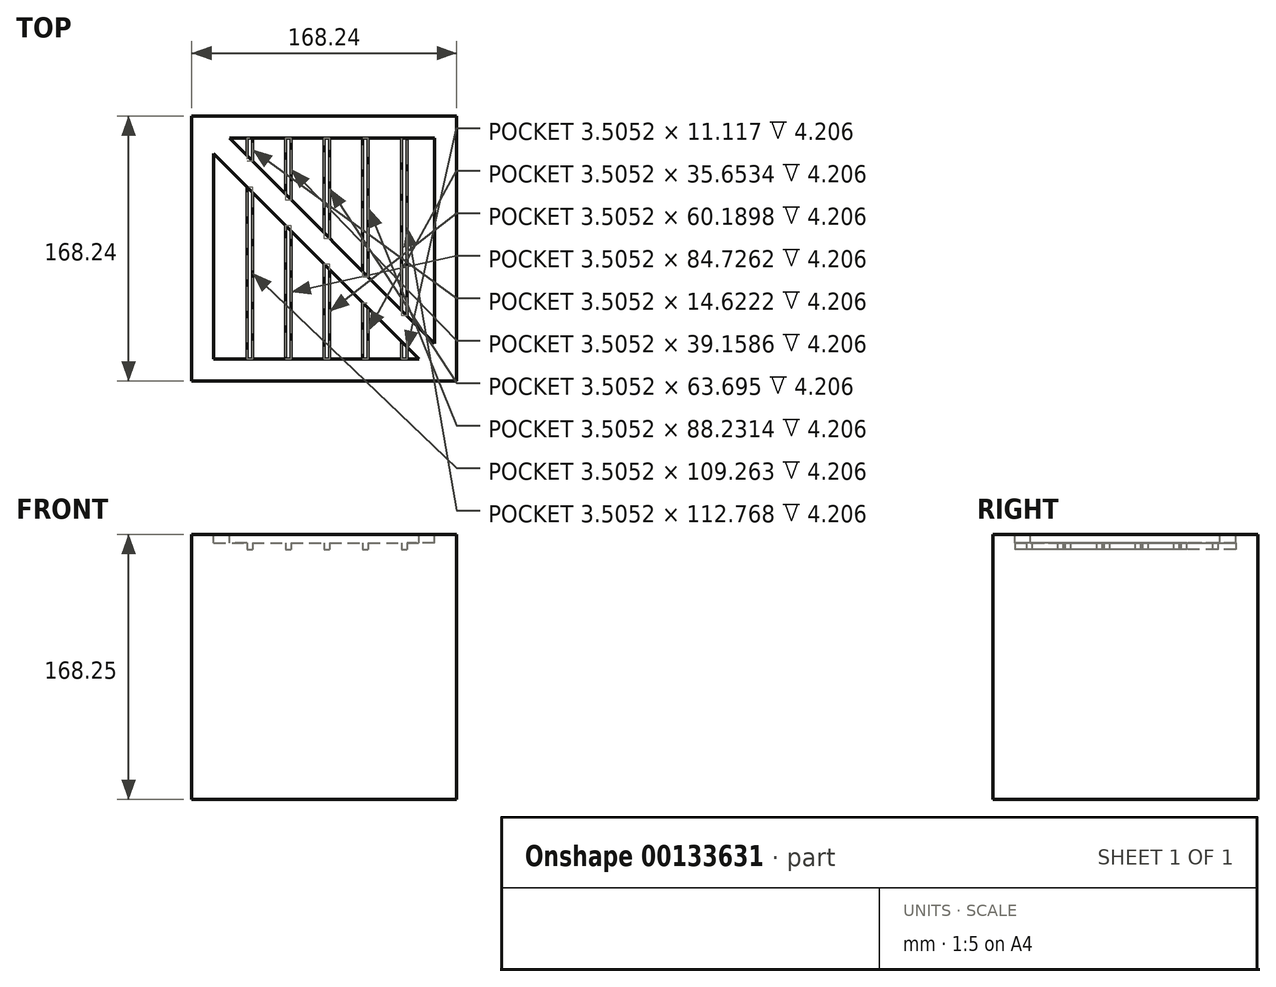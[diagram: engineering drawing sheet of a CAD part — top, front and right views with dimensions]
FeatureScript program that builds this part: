
annotation { "Feature Type Name" : "Feature", "Feature Type Description" : "" }
export const myFeature = defineFeature(function(context is Context, id is Id, definition is map)
    precondition{}
    {
        {
            var Q0;
            Q0=qCreatedBy(makeId("Top.planeOp"),FACE);
            var sketch = newSketch(context, id + "F0", { "sketchPlane" : qUnion([Q0])});
            skLineSegment(sketch, "E0.bottom", {"start": v(609.6, 609.6) * mm, "end": v(-609.6, 609.6) * mm});
            skLineSegment(sketch, "E0.top", {"start": v(609.6, -609.6) * mm, "end": v(-609.6, -609.6) * mm});
            skLineSegment(sketch, "E0.left", {"start": v(609.6, 609.6) * mm, "end": v(609.6, -609.6) * mm});
            skLineSegment(sketch, "E0.right", {"start": v(-609.6, 609.6) * mm, "end": v(-609.6, -609.6) * mm});
            skPoint(sketch, "E0.middle", {"position": v(0, 0) * mm});
            skSolve(sketch);
        }
        {
            var Q0;
            Q0=qSketchRegion(id+"F0",true);
            extrude(context, id + "F1", {"entities" : qUnion([Q0]), "flatOperationType" : FlatOperationType.REMOVE, "offsetDistance" : 30.48 * mm, "depth" : 1219.2 * mm, "domain" : OperationDomain.MODEL});
        }
        {
            var Q0;
            Q0=makeQuery(id+"F1.opExtrude","CAP_FACE",FACE,{"disambiguationData":[OSD([sQuery(id+"F0.wireOp",EDGE,"E0.bottom"),sQuery(id+"F0.wireOp",EDGE,"E0.top"),sQuery(id+"F0.wireOp",EDGE,"E0.left"),sQuery(id+"F0.wireOp",EDGE,"E0.right")])],"isStart":false});
            var sketch = newSketch(context, id + "F2", { "sketchPlane" : qUnion([Q0])});
            skLineSegment(sketch, "E1.0", {"start": v(508, -508) * mm, "end": v(508, 508) * mm});
            skLineSegment(sketch, "E1.1", {"start": v(-508, -508) * mm, "end": v(508, -508) * mm});
            skLineSegment(sketch, "E1.2", {"start": v(-508, 508) * mm, "end": v(-508, -508) * mm});
            skLineSegment(sketch, "E1.3", {"start": v(508, 508) * mm, "end": v(-508, 508) * mm});
            skSolve(sketch);
        }
        {
            var Q0;
            Q0=qSketchRegion(id+"F2",true);
            extrude(context, id + "F3", {"entities" : qUnion([Q0]), "operationType" : NewBodyOperationType.REMOVE, "flatOperationType" : FlatOperationType.REMOVE, "oppositeDirection" : true, "offsetDistance" : 30.48 * mm, "depth" : 69.85 * mm, "domain" : OperationDomain.MODEL});
        }
        {
            var Q0;
            Q0=makeQuery(id+"F1.opExtrude","CAP_FACE",FACE,{"disambiguationData":[OSD([sQuery(id+"F0.wireOp",EDGE,"E0.bottom"),sQuery(id+"F0.wireOp",EDGE,"E0.top"),sQuery(id+"F0.wireOp",EDGE,"E0.left"),sQuery(id+"F0.wireOp",EDGE,"E0.right")])],"isStart":false});
            var sketch = newSketch(context, id + "F4", { "sketchPlane" : qUnion([Q0])});
            skLineSegment(sketch, "E2", {"start": v(-436.16, 508) * mm, "end": v(508, -436.16) * mm});
            skLineSegment(sketch, "E3", {"start": v(-508, 436.16) * mm, "end": v(436.16, -508) * mm});
            skLineSegment(sketch, "E4", {"start": v(-436.16, 508) * mm, "end": v(-508, 508) * mm});
            skLineSegment(sketch, "E5", {"start": v(-508, 508) * mm, "end": v(-508, 436.16) * mm});
            skLineSegment(sketch, "E6", {"start": v(436.16, -508) * mm, "end": v(508, -508) * mm});
            skLineSegment(sketch, "E7", {"start": v(508, -508) * mm, "end": v(508, -436.16) * mm});
            skSolve(sketch);
        }
        {
            var Q0;
            Q0=makeQuery(id+"F4.imprint","IMPRINT",FACE,{"disambiguationData":[TD([[makeQuery(id+"F4.imprint","IMPRINT",EDGE,{"derivedFrom":sQuery(id+"F4.wireOp",EDGE,"E2")}),-1.0]])]});
            extrude(context, id + "F5", {"entities" : qUnion([Q0]), "oppositeDirection" : true, "depth" : 69.85 * mm});
        }
        {
            var Q0;
            Q0=makeQuery(id+"F3.boolean.opBoolean","COPY",FACE,{"derivedFrom":makeQuery(id+"F3.opExtrude","CAP_FACE",FACE,{"disambiguationData":[OSD([sQuery(id+"F2.wireOp",EDGE,"E1.0"),sQuery(id+"F2.wireOp",EDGE,"E1.1"),sQuery(id+"F2.wireOp",EDGE,"E1.2"),sQuery(id+"F2.wireOp",EDGE,"E1.3")])],"isStart":false})});
            var sketch = newSketch(context, id + "F6", { "sketchPlane" : qUnion([Q0])});
            skLineSegment(sketch, "E8.bottom", {"start": v(-508, 508) * mm, "end": v(-355.6, 508) * mm});
            skLineSegment(sketch, "E8.top", {"start": v(-508, -508) * mm, "end": v(-355.6, -508) * mm});
            skLineSegment(sketch, "E8.left", {"start": v(-508, 508) * mm, "end": v(-508, -508) * mm});
            skLineSegment(sketch, "E8.right", {"start": v(-355.6, 508) * mm, "end": v(-355.6, -508) * mm});
            skLineSegment(sketch, "E9.1.0.0", {"start": v(-330.2, 508) * mm, "end": v(-330.2, -508) * mm});
            skLineSegment(sketch, "E9.1.0.1", {"start": v(-177.8, 508) * mm, "end": v(-177.8, -508) * mm});
            skLineSegment(sketch, "E9.2.0.0", {"start": v(-152.4, 508) * mm, "end": v(-152.4, -508) * mm});
            skLineSegment(sketch, "E9.2.0.1", {"start": v(0, 508) * mm, "end": v(0, -508) * mm});
            skLineSegment(sketch, "E9.3.0.0", {"start": v(25.4, 508) * mm, "end": v(25.4, -508) * mm});
            skLineSegment(sketch, "E9.3.0.1", {"start": v(177.8, 508) * mm, "end": v(177.8, -508) * mm});
            skLineSegment(sketch, "E9.4.0.0", {"start": v(203.2, 508) * mm, "end": v(203.2, -508) * mm});
            skLineSegment(sketch, "E9.4.0.1", {"start": v(355.6, 508) * mm, "end": v(355.6, -508) * mm});
            skLineSegment(sketch, "E9.5.0.0", {"start": v(381, 508) * mm, "end": v(381, -508) * mm});
            skLineSegment(sketch, "E9.5.0.1", {"start": v(533.4, 508) * mm, "end": v(533.4, -508) * mm});
            skLineSegment(sketch, "E9.direction1", {"start": v(-508, -508) * mm, "end": v(-330.2, -508) * mm, "construction": true});
            skSolve(sketch);
        }
        {
            var Q0;
            Q0=qSketchRegion(id+"F6",true);
            var Q1;
            {var subQ0=sQuery(id+"F6.wireOp",EDGE,"E9.1.0.0");Q1=makeQuery(id+"F6.imprint","IMPRINT",FACE,{"disambiguationData":[TD([[makeQuery(id+"F6.imprint","IMPRINT",EDGE,{"derivedFrom":subQ0}),1.0]])]});}
            var Q2;
            {var subQ0=sQuery(id+"F6.wireOp",EDGE,"E9.2.0.0");Q2=makeQuery(id+"F6.imprint","IMPRINT",FACE,{"disambiguationData":[TD([[makeQuery(id+"F6.imprint","IMPRINT",EDGE,{"derivedFrom":subQ0}),1.0]])]});}
            var Q3;
            {var subQ0=sQuery(id+"F6.wireOp",EDGE,"E9.3.0.0");Q3=makeQuery(id+"F6.imprint","IMPRINT",FACE,{"disambiguationData":[TD([[makeQuery(id+"F6.imprint","IMPRINT",EDGE,{"derivedFrom":subQ0}),1.0]])]});}
            var Q4;
            {var subQ0=sQuery(id+"F6.wireOp",EDGE,"E9.4.0.0");Q4=makeQuery(id+"F6.imprint","IMPRINT",FACE,{"disambiguationData":[TD([[makeQuery(id+"F6.imprint","IMPRINT",EDGE,{"derivedFrom":subQ0}),1.0]])]});}
            var Q5;
            {var subQ0=sQuery(id+"F6.wireOp",EDGE,"E9.5.0.0");Q5=makeQuery(id+"F6.imprint","IMPRINT",FACE,{"disambiguationData":[TD([[makeQuery(id+"F6.imprint","IMPRINT",EDGE,{"derivedFrom":subQ0}),1.0]])]});}
            extrude(context, id + "F7", {"entities" : qUnion([Q0, Q1, Q2, Q3, Q4, Q5]), "operationType" : NewBodyOperationType.ADD, "depth" : 30.48 * mm});
        }
        {
            var Q0;
            Q0=makeQuery(id+"F7.boolean.opBoolean","MERGE",FACE,{"derivedFrom":[makeQuery(id+"F1.opExtrude","CAP_FACE",FACE,{"disambiguationData":[OSD([sQuery(id+"F0.wireOp",EDGE,"E0.bottom"),sQuery(id+"F0.wireOp",EDGE,"E0.top"),sQuery(id+"F0.wireOp",EDGE,"E0.left"),sQuery(id+"F0.wireOp",EDGE,"E0.right")])],"isStart":false}),makeQuery(id+"F5.opExtrude","CAP_FACE",FACE,{"disambiguationData":[OSD([sQuery(id+"F4.wireOp",EDGE,"E2"),sQuery(id+"F4.wireOp",EDGE,"E3"),sQuery(id+"F4.wireOp",EDGE,"E4"),sQuery(id+"F4.wireOp",EDGE,"E5"),sQuery(id+"F4.wireOp",EDGE,"E6"),sQuery(id+"F4.wireOp",EDGE,"E7")])],"isStart":true})]});
            cPlane(context, id + "F8", {"entities" : qUnion([Q0]), "cplaneType" : CPlaneType.OFFSET, "offset" : 609.6 * mm, "oppositeDirection" : true, "width" : 152.4 * mm, "height" : 152.4 * mm});
        }
        {
            var Q0;
            Q0=qCreatedBy(id+"F8.planeOp",FACE);
            var sketch = newSketch(context, id + "F9", { "sketchPlane" : qUnion([Q0])});
            skLineSegment(sketch, "E10", {"start": v(0, 0) * mm, "end": v(-960.31, 0) * mm});
            skLineSegment(sketch, "E11", {"start": v(0, 0) * mm, "end": v(0, -833.57) * mm});
            skSolve(sketch);
        }
        {
            var Q0;
            Q0=makeQuery(id+"F1.opExtrude","SWEPT_BODY",BODY,{"disambiguationData":[OSD([sQuery(id+"F0.wireOp",EDGE,"E0.bottom"),sQuery(id+"F0.wireOp",EDGE,"E0.top"),sQuery(id+"F0.wireOp",EDGE,"E0.left"),sQuery(id+"F0.wireOp",EDGE,"E0.right")])]});
            var Q1;
            Q1=qCreatedBy(makeId("Origin.pointOp"),VERTEX);
            transform(context, id + "F10", {"entities" : qUnion([Q0]), "transformType" : TransformType.SCALE_UNIFORMLY, "scale" : .138, "scalePoint" : qUnion([Q1]), "makeCopy" : false});
        }
    });
